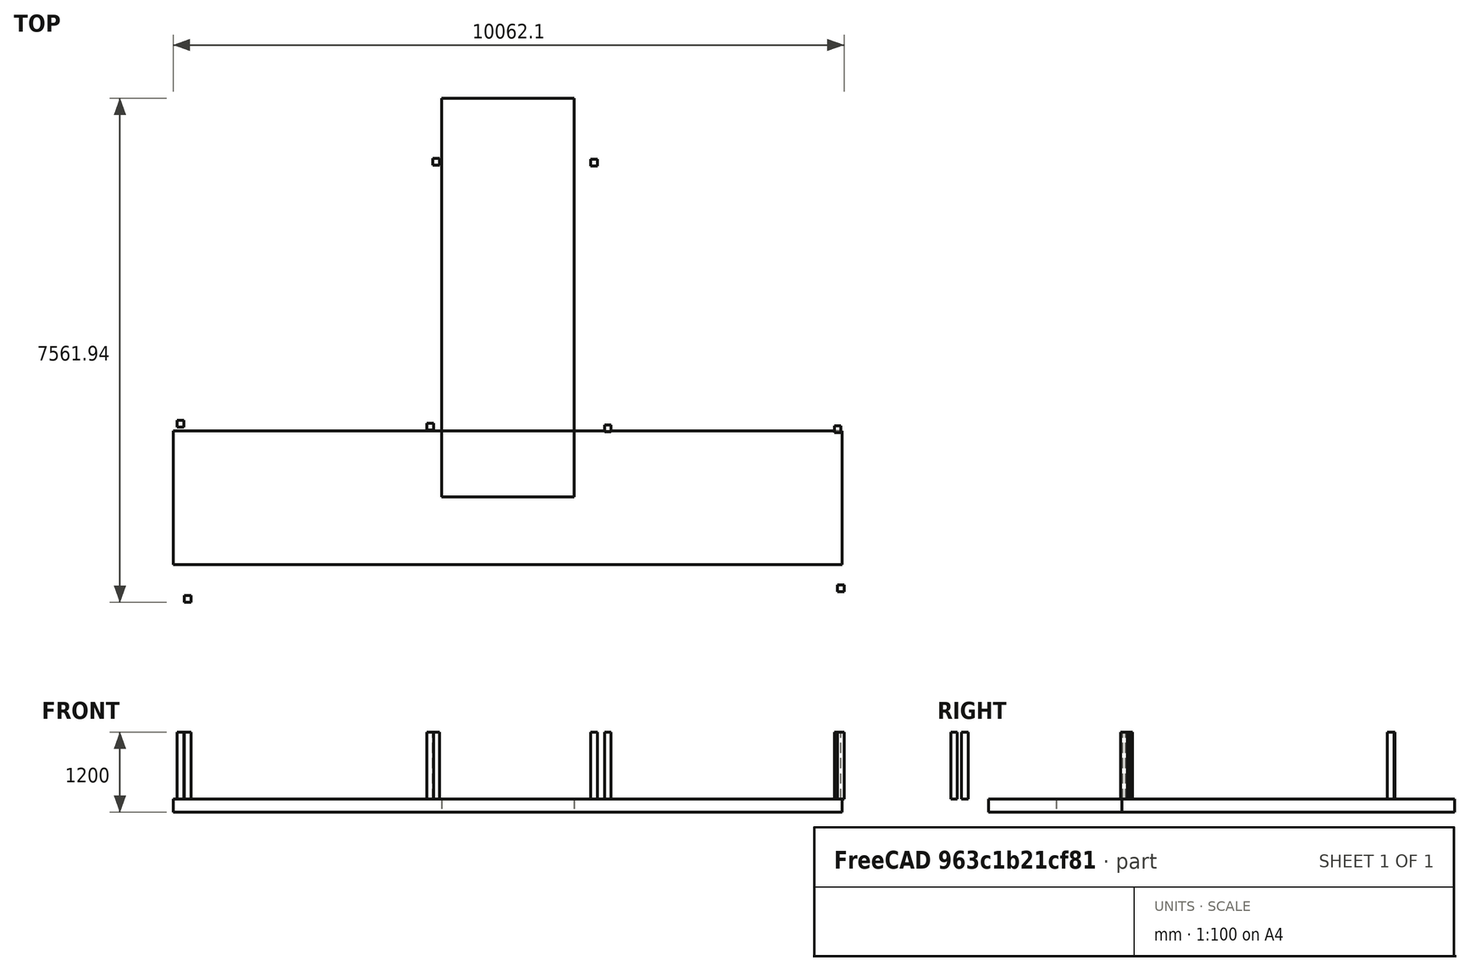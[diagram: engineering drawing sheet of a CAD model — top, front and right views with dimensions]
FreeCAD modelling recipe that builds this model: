
FCSTD DOCUMENT  (FreeCAD 1.0R39285 (Git))
Label: flydebro
License: All rights reserved
objects: Part::FeaturePython×10, Part::Part2DObjectPython×2
note: 12 computed .brp shape members not serialized (recipe doc carries the construction recipe); baked Part::Feature solids carry a one-line shape summary decoded from their .brp

FEATURE [Part::Part2DObjectPython] Rectangle  # Draft 2D object (typed FeaturePython)
  Area = 1.18883e+07
  ChamferSize = 0
  Columns = 1
  FilletRadius = 0
  Height = 5979.13
  Length = 1988.3
  MakeFace = true
  Placement = pos=(-986.646,-997.588,0) rot=(0,0,1;0rad)
  Rows = 1
FEATURE [Part::Part2DObjectPython] Rectangle001  # Draft 2D object (typed FeaturePython)
  Area = 2.00866e+07
  ChamferSize = 0
  Columns = 1
  FilletRadius = 0
  Height = 2002.48
  Length = 10030.9
  MakeFace = true
  Placement = pos=(-5014.28,-2013.2,0) rot=(0,0,1;0rad)
  Rows = 1
FEATURE [Part::FeaturePython] Structure  label="Slab"  # Arch/BIM 118 (typed FeaturePython)
  Base = -> Rectangle001
  BaseMirror = false
  BaseOffsetX = 0
  BaseOffsetY = 0
  BasePerpendicularToTool = false
  BaseRotation = 0
  ComputedLength = 200
  FaceMaker = 0
  Height = 200
  HorizontalArea = 2.00866e+07
  IfcData = attributes={"GlobalId": {"name": "GlobalId", "type": "IfcGloballyUniqueId", "is_enum": false, "enum_values": []}, "Description": {"... (+453 chars omitted),+1 more (map truncated)
  IfcType = 118
  Length = 2002.48
  MoveBase = false
  MoveWithHost = false
  Nodes = (4) [(-5014.28,-2013.2,0),(5016.6,-2013.2,0),(5016.6,-10.7155,0),(-5014.28,-10.7155,0)]
  NodesOffset = 0
  Normal = (0,0,-1)
  PerimeterLength = 24066.7
  PredefinedType = 0
  ToolOffsetFirst = 0
  ToolOffsetLast = 0
  VerticalArea = 4.81335e+06
  Width = 10030.9
FEATURE [Part::FeaturePython] Structure001  label="Slab001"  # Arch/BIM 118 (typed FeaturePython)
  Base = -> Rectangle
  BaseMirror = false
  BaseOffsetX = 0
  BaseOffsetY = 0
  BasePerpendicularToTool = false
  BaseRotation = 0
  ComputedLength = 200
  FaceMaker = 0
  Height = 200
  HorizontalArea = 1.18883e+07
  IfcData = attributes={"GlobalId": {"name": "GlobalId", "type": "IfcGloballyUniqueId", "is_enum": false, "enum_values": []}, "Description": {"... (+453 chars omitted),+1 more (map truncated)
  IfcType = 118
  Length = 5979.13
  MoveBase = false
  MoveWithHost = false
  Nodes = (4) [(-986.646,-997.588,0),(1001.66,-997.588,0),(1001.66,4981.54,0),(-986.646,4981.54,0)]
  NodesOffset = 0
  Normal = (0,0,-1)
  PerimeterLength = 15934.9
  PredefinedType = 0
  ToolOffsetFirst = 0
  ToolOffsetLast = 0
  VerticalArea = 3.18697e+06
  Width = 1988.3
FEATURE [Part::FeaturePython] Structure002  label="Column"  # Arch/BIM 24 (typed FeaturePython)
  BaseMirror = false
  BaseOffsetX = 0
  BaseOffsetY = 0
  BasePerpendicularToTool = false
  BaseRotation = 0
  ComputedLength = 1000
  FaceMaker = 0
  Height = 1000
  HorizontalArea = 10000
  IfcData = attributes={"GlobalId": {"name": "GlobalId", "type": "IfcGloballyUniqueId", "is_enum": false, "enum_values": []}, "Description": {"... (+438 chars omitted),+1 more (map truncated)
  IfcType = 24
  Length = 100
  MoveBase = false
  MoveWithHost = false
  Nodes = (2) [(-3.88578e-16,0,0),(-3.88578e-16,0,1000)]
  NodesOffset = 0
  Normal = (0,0,0)
  PerimeterLength = 400
  Placement = pos=(-4799.11,-2530.4,1.42e-14) rot=(0,0,1;0rad)
  PredefinedType = 0
  ToolOffsetFirst = 0
  ToolOffsetLast = 0
  VerticalArea = 400000
  Width = 100
FEATURE [Part::FeaturePython] Structure003  label="Column001"  # Arch/BIM 24 (typed FeaturePython)
  BaseMirror = false
  BaseOffsetX = 0
  BaseOffsetY = 0
  BasePerpendicularToTool = false
  BaseRotation = 0
  ComputedLength = 1000
  FaceMaker = 0
  Height = 1000
  HorizontalArea = 10000
  IfcData = attributes={"GlobalId": {"name": "GlobalId", "type": "IfcGloballyUniqueId", "is_enum": false, "enum_values": []}, "Description": {"... (+438 chars omitted),+1 more (map truncated)
  IfcType = 24
  Length = 100
  MoveBase = false
  MoveWithHost = false
  Nodes = (2) [(-3.88578e-16,0,0),(-3.88578e-16,0,1000)]
  NodesOffset = 0
  Normal = (0,0,0)
  PerimeterLength = 400
  Placement = pos=(-4905.62,97.9999,0) rot=(0,0,1;0rad)
  PredefinedType = 0
  ToolOffsetFirst = 0
  ToolOffsetLast = 0
  VerticalArea = 400000
  Width = 100
FEATURE [Part::FeaturePython] Structure004  label="Column002"  # Arch/BIM 24 (typed FeaturePython)
  BaseMirror = false
  BaseOffsetX = 0
  BaseOffsetY = 0
  BasePerpendicularToTool = false
  BaseRotation = 0
  ComputedLength = 1000
  FaceMaker = 0
  Height = 1000
  HorizontalArea = 10000
  IfcData = attributes={"GlobalId": {"name": "GlobalId", "type": "IfcGloballyUniqueId", "is_enum": false, "enum_values": []}, "Description": {"... (+438 chars omitted),+1 more (map truncated)
  IfcType = 24
  Length = 100
  MoveBase = false
  MoveWithHost = false
  Nodes = (2) [(-3.88578e-16,0,0),(-3.88578e-16,0,1000)]
  NodesOffset = 0
  Normal = (0,0,0)
  PerimeterLength = 400
  Placement = pos=(4951.4,18.315,0) rot=(0,0,1;0rad)
  PredefinedType = 0
  ToolOffsetFirst = 0
  ToolOffsetLast = 0
  VerticalArea = 400000
  Width = 100
FEATURE [Part::FeaturePython] Structure005  label="Column003"  # Arch/BIM 24 (typed FeaturePython)
  BaseMirror = false
  BaseOffsetX = 0
  BaseOffsetY = 0
  BasePerpendicularToTool = false
  BaseRotation = 0
  ComputedLength = 1000
  FaceMaker = 0
  Height = 1000
  HorizontalArea = 10000
  IfcData = attributes={"GlobalId": {"name": "GlobalId", "type": "IfcGloballyUniqueId", "is_enum": false, "enum_values": []}, "Description": {"... (+438 chars omitted),+1 more (map truncated)
  IfcType = 24
  Length = 100
  MoveBase = false
  MoveWithHost = false
  Nodes = (2) [(-3.88578e-16,0,0),(-3.88578e-16,0,1000)]
  NodesOffset = 0
  Normal = (0,0,0)
  PerimeterLength = 400
  Placement = pos=(4997.8,-2368.91,0) rot=(0,0,1;0rad)
  PredefinedType = 0
  ToolOffsetFirst = 0
  ToolOffsetLast = 0
  VerticalArea = 400000
  Width = 100
FEATURE [Part::FeaturePython] Structure006  label="Column004"  # Arch/BIM 24 (typed FeaturePython)
  BaseMirror = false
  BaseOffsetX = 0
  BaseOffsetY = 0
  BasePerpendicularToTool = false
  BaseRotation = 0
  ComputedLength = 1000
  FaceMaker = 0
  Height = 1000
  HorizontalArea = 10000
  IfcData = attributes={"GlobalId": {"name": "GlobalId", "type": "IfcGloballyUniqueId", "is_enum": false, "enum_values": []}, "Description": {"... (+438 chars omitted),+1 more (map truncated)
  IfcType = 24
  Length = 100
  MoveBase = false
  MoveWithHost = false
  Nodes = (2) [(-3.88578e-16,0,0),(-3.88578e-16,0,1000)]
  NodesOffset = 0
  Normal = (0,0,0)
  PerimeterLength = 400
  Placement = pos=(-1160.9,52.9179,0) rot=(0,0,1;0rad)
  PredefinedType = 0
  ToolOffsetFirst = 0
  ToolOffsetLast = 0
  VerticalArea = 400000
  Width = 100
FEATURE [Part::FeaturePython] Structure007  label="Column005"  # Arch/BIM 24 (typed FeaturePython)
  BaseMirror = false
  BaseOffsetX = 0
  BaseOffsetY = 0
  BasePerpendicularToTool = false
  BaseRotation = 0
  ComputedLength = 1000
  FaceMaker = 0
  Height = 1000
  HorizontalArea = 10000
  IfcData = attributes={"GlobalId": {"name": "GlobalId", "type": "IfcGloballyUniqueId", "is_enum": false, "enum_values": []}, "Description": {"... (+438 chars omitted),+1 more (map truncated)
  IfcType = 24
  Length = 100
  MoveBase = false
  MoveWithHost = false
  Nodes = (2) [(-3.88578e-16,0,0),(-3.88578e-16,0,1000)]
  NodesOffset = 0
  Normal = (0,0,0)
  PerimeterLength = 400
  Placement = pos=(1503.97,28.1222,0) rot=(0,0,1;0rad)
  PredefinedType = 0
  ToolOffsetFirst = 0
  ToolOffsetLast = 0
  VerticalArea = 400000
  Width = 100
FEATURE [Part::FeaturePython] Structure009  label="Column007"  # Arch/BIM 24 (typed FeaturePython)
  BaseMirror = false
  BaseOffsetX = 0
  BaseOffsetY = 0
  BasePerpendicularToTool = false
  BaseRotation = 0
  ComputedLength = 1000
  FaceMaker = 0
  Height = 1000
  HorizontalArea = 10000
  IfcData = attributes={"GlobalId": {"name": "GlobalId", "type": "IfcGloballyUniqueId", "is_enum": false, "enum_values": []}, "Description": {"... (+438 chars omitted),+1 more (map truncated)
  IfcType = 24
  Length = 100
  MoveBase = false
  MoveWithHost = false
  Nodes = (2) [(-3.88578e-16,0,0),(-3.88578e-16,0,1000)]
  NodesOffset = 0
  Normal = (0,0,0)
  PerimeterLength = 400
  Placement = pos=(1297.04,4019.02,0) rot=(0,0,1;0rad)
  PredefinedType = 0
  ToolOffsetFirst = 0
  ToolOffsetLast = 0
  VerticalArea = 400000
  Width = 100
FEATURE [Part::FeaturePython] Structure010  label="Column008"  # Arch/BIM 24 (typed FeaturePython)
  BaseMirror = false
  BaseOffsetX = 0
  BaseOffsetY = 0
  BasePerpendicularToTool = false
  BaseRotation = 0
  ComputedLength = 1000
  FaceMaker = 0
  Height = 1000
  HorizontalArea = 10000
  IfcData = attributes={"GlobalId": {"name": "GlobalId", "type": "IfcGloballyUniqueId", "is_enum": false, "enum_values": []}, "Description": {"... (+438 chars omitted),+1 more (map truncated)
  IfcType = 24
  Length = 100
  MoveBase = false
  MoveWithHost = false
  Nodes = (2) [(-3.88578e-16,0,0),(-3.88578e-16,0,1000)]
  NodesOffset = 0
  Normal = (0,0,0)
  PerimeterLength = 400
  Placement = pos=(-1070.61,4031.49,2.274e-13) rot=(0,0,1;0rad)
  PredefinedType = 0
  ToolOffsetFirst = 0
  ToolOffsetLast = 0
  VerticalArea = 400000
  Width = 100
